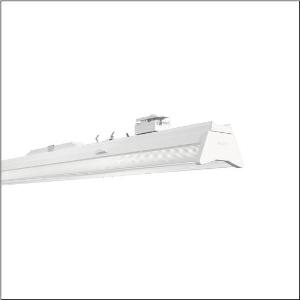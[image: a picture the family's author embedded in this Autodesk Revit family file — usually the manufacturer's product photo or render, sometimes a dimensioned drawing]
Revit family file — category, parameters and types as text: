
# Revit family: licross_r__21_performance_mo_52tm16dn445g_a9c4
name_source: partatom
category: Lighting Fixtures
units: mm (PartAtom-declared; Revit-internal decimal feet)

## family parameters
Cut with Voids When Loaded = No
Host = Face
Light Source = No
Part Type = Normal
Room Calculation Point = No
Round Connector Dimension = Use Diameter
Shared = No

## types (1)
- --- (1 x LED, 4500 lm, 24.9 W, 4000K)
    Apparent Load = 25 VA
    CIE Flux Codes = 66 88 96 79 100
    Color Rendering = 80
    Color Temperature = 4000K
    Default Elevation = 1800 mm
    Description = Licross® 21 Performance MO, luminaire insert, of sheet steel, galvanised, coil coated, white, length: 1.500mm, width: 120mm, height: 123mm, LED rated luminous flux: 4.500lm, light colour: 840, control gear: DALI 2, with plug, 5-pole, with phase selection, mains connection: 220..240V, AC, 50/60Hz, rated input power: 25W, halogen-free wiring, primary light control with lens, of plastic, primary optical cover: cover, of PMMA, CAT 2 (L<= 3000cd/m²), light emission: direct/indirect distribution, primary light characteristic: symmetric, protection rating (complete): IP40, insulation class (complete): insulation class I (protective earthing), certification: CE, ENEC, UKCA, protection symbol: D if used in an environment without relevant dust loads with corresponding accessories, impact resistance: IK06, permissible ambient temperature for indoor applications: -25..+50°C, corresponds to IFS (International Featured Standards) requirements for safety and quality in the food industry, reducing of maximum allowable ambient temperature of 5°C with ceiling mounting, LABS conformity tested according to VDMA 24364:2018-05, packaging unit: 1 piece
    Height = 114 mm
    Lamp = 1 x LED
    Lamp Light Flux = 4500 lm
    Lamp Power = 24.9 W
    Lamp count = 1
    Length = 1500 mm
    Luminous efficacy = 181 lm/W
    Manufacturer = Siteco
    ModVariant = No
    Model = 52TM16DN445G
    Mounting Place = Ceiling
    Mounting Type = Pendant
    Number of Poles = 1
    OnlyDefault = Yes
    Power Factor = 1
    Product Name = Licross® 21 Performance MO
    Product group = luminaire insert
    ProductGroupID = 901
    Protection Class = Protection class I
    Protection Degree = IP 40
    RLX_Detail_Level = 1
    RLX_Emergency_Light_Flux = 0 lm
    RLX_Emergency_Type = 0
    RLX_Emergency_Type_DB = No
    RlxData = <blob elided: 33537 chars, md5=f7d64086>
    Socket = socket
    Standby Power = 0 W
    System Light Flux = 4500 lm
    System Power = 25 W
    Type Comments = factory setting: luminous flux: 100 % | dim-lin: 254 | 165 mA
    Type Image = l_1256138.jpg
    URL = http://relux.com
    VarID = @adj_006967
    Voltage = 0 V
    Weight = 0.00 kg
    Width = 120 mm

## geometry (parser evidence)
native form markers: Blend x4, Sweep x11
no freeform markers — native parametric forms only
